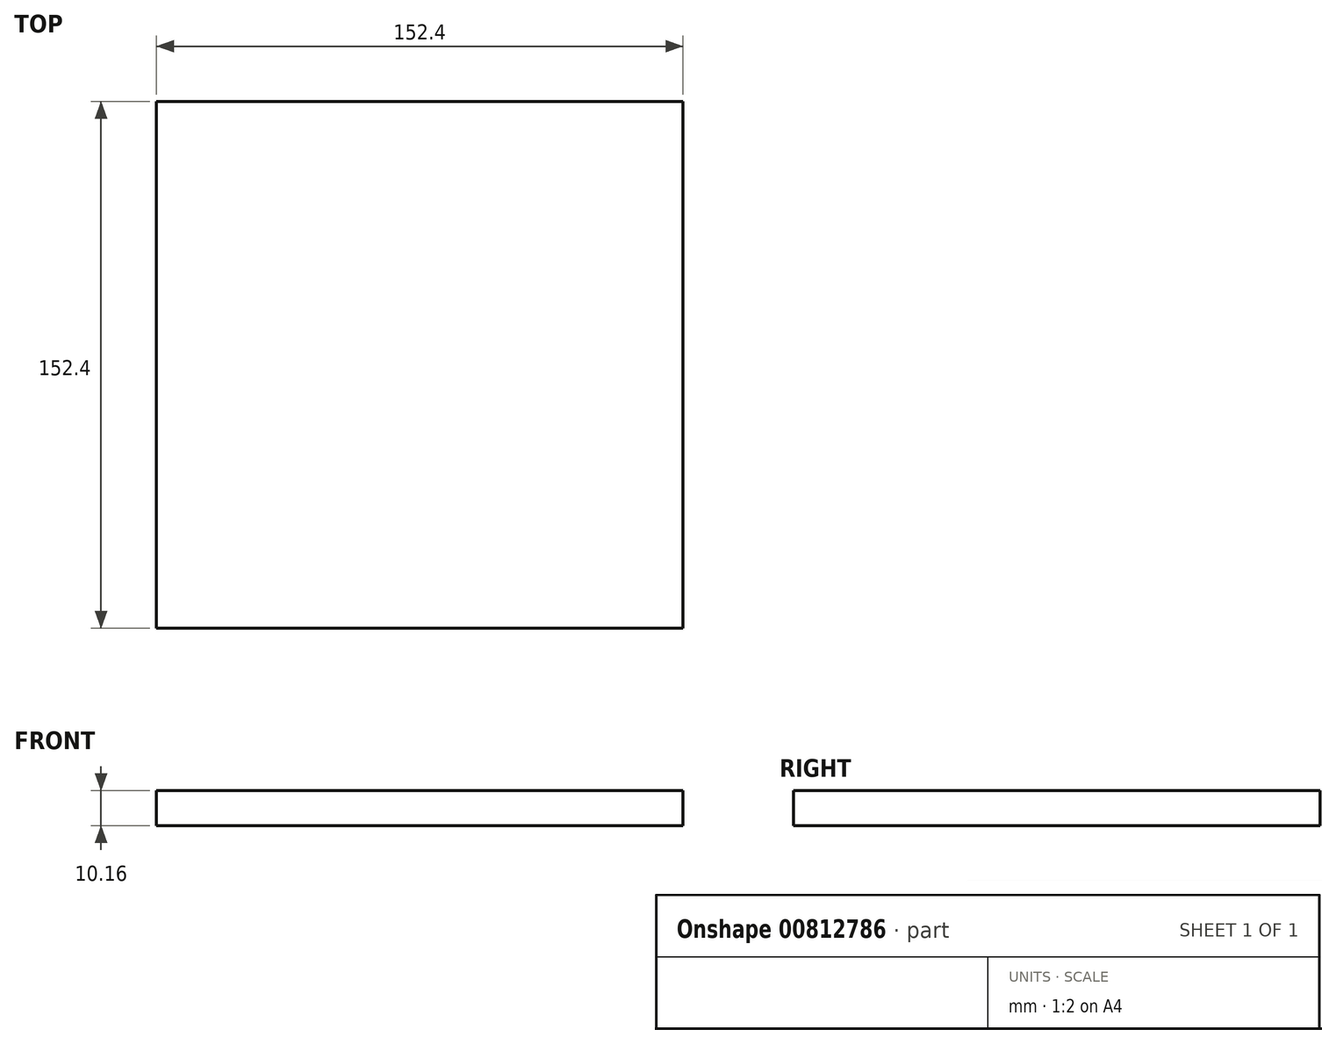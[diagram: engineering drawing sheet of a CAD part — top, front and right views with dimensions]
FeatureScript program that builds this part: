
annotation { "Feature Type Name" : "Feature", "Feature Type Description" : "" }
export const myFeature = defineFeature(function(context is Context, id is Id, definition is map)
    precondition{}
    {
        {
            var Q0;
            Q0=qCreatedBy(makeId("Top.planeOp"),FACE);
            var sketch = newSketch(context, id + "F0", { "sketchPlane" : qUnion([Q0])});
            skLineSegment(sketch, "E0.bottom", {"start": v(0, 0) * mm, "end": v(-152.4, 0) * mm});
            skLineSegment(sketch, "E0.top", {"start": v(0, -152.4) * mm, "end": v(-152.4, -152.4) * mm});
            skLineSegment(sketch, "E0.left", {"start": v(0, 0) * mm, "end": v(0, -152.4) * mm});
            skLineSegment(sketch, "E0.right", {"start": v(-152.4, 0) * mm, "end": v(-152.4, -152.4) * mm});
            skSolve(sketch);
        }
        {
            var Q0;
            Q0=makeQuery(id+"F0.imprint","IMPRINT",FACE,{"disambiguationData":[TD([[makeQuery(id+"F0.imprint","IMPRINT",EDGE,{"derivedFrom":sQuery(id+"F0.wireOp",EDGE,"E0.bottom")}),1.0]])]});
            extrude(context, id + "F1", {"entities" : qUnion([Q0]), "endBound" : BoundingType.SYMMETRIC, "depth" : 10.16 * mm, "offsetDistance" : 25.4 * mm});
        }
    });
